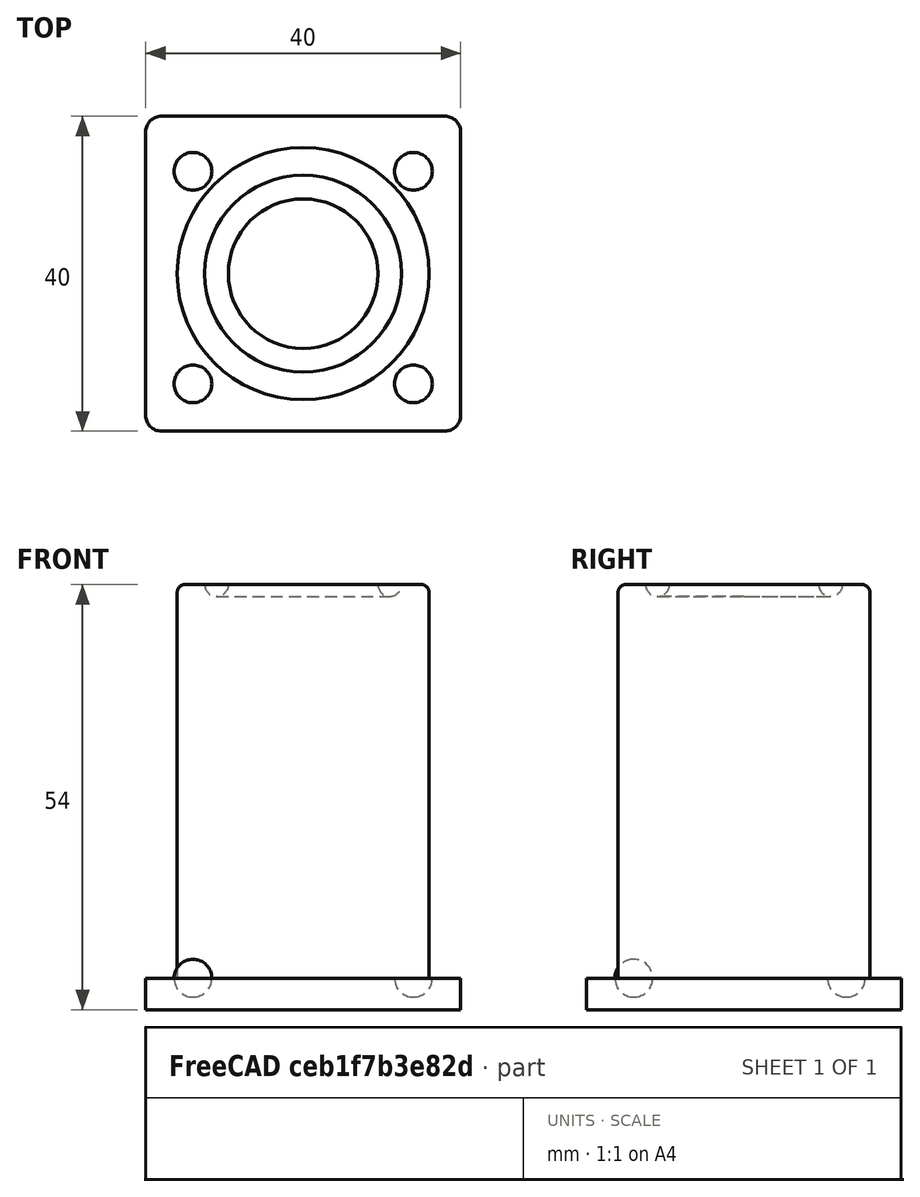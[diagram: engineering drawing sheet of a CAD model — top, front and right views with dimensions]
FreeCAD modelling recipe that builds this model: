
FCSTD DOCUMENT  (FreeCAD 1.0R39319 (Git))
Label: ojt1_t15r03_table_leg
License: All rights reserved
LicenseURL: https://en.wikipedia.org/wiki/All_rights_reserved
objects: Part::Fillet×2, Part::Cut×2, Part::Box×1, Part::Sphere×1, Part::FeaturePython×1, Part::Cylinder×1, Part::Torus×1, Part::MultiFuse×1
note: 9 computed .brp shape members not serialized (recipe doc carries the construction recipe); baked Part::Feature solids carry a one-line shape summary decoded from their .brp

FEATURE [Part::Box] Box  label="Cub"
  AttacherType = Attacher::AttachEngine3D
  Height = 4
  Length = 40
  Width = 40
FEATURE [Part::Fillet] Fillet
  Base = -> Box
  EdgeLinks = -> Box [Edge1,Edge3,Edge5,Edge7]
  Edges = 4 edges r=2: [Edge1,Edge3,Edge5,Edge7]
FEATURE [Part::Sphere] Sphere  label="Esfera"
  Angle1 = -90
  Angle2 = 90
  Angle3 = 360
  AttacherType = Attacher::AttachEngine3D
  Placement = pos=(6,6,4) rot=(0,0,1;0rad)
  Radius = 2.4
FEATURE [Part::FeaturePython] Array  # Draft array (typed FeaturePython)
  AlwaysSyncPlacement = false
  Angle = 360
  ArrayType = 0
  Axis = (0,0,1)
  Base = -> Sphere
  Center = (0,0,0)
  Count = 4
  ExpandArray = false
  Fuse = false
  IntervalAxis = (0,0,0)
  IntervalX = (28,0,0)
  IntervalY = (0,27,0)
  IntervalZ = (0,0,100)
  NumberCircles = 3
  NumberPolar = 5
  NumberX = 2
  NumberY = 2
  NumberZ = 1
  PlacementList = 4 placements: [(6,6,4),(6,33,4),(34,6,4),(34,33,4)]
  RadialDistance = 50
  ScaleList = (4) [(1,1,1),(1,1,1),(1,1,1),(1,1,1)]
  Symmetry = 1
  TangentialDistance = 25
FEATURE [Part::Cut] Cut
  Base = -> Fillet
  Refine = true
  Tool = -> Array
FEATURE [Part::Cylinder] Cylinder  label="Cilindre"
  Angle = 360
  AttacherType = Attacher::AttachEngine3D
  FirstAngle = 0
  Height = 50
  Placement = pos=(20,20,4) rot=(0,0,1;0rad)
  Radius = 16
  SecondAngle = 0
FEATURE [Part::Fillet] Fillet001
  Base = -> Cylinder
  EdgeLinks = -> Cylinder [Edge3]
  Edges = 1 edges r=1: [Edge3]
FEATURE [Part::Torus] Torus
  Angle1 = -180
  Angle2 = 180
  Angle3 = 360
  AttacherType = Attacher::AttachEngine3D
  Placement = pos=(20,20,54) rot=(0,0,1;0rad)
  Radius1 = 11
  Radius2 = 1.5
FEATURE [Part::Cut] Cut001
  Base = -> Fillet001
  Refine = true
  Tool = -> Torus
FEATURE [Part::MultiFuse] Fusion
  Refine = true
  Shapes = -> [Cut,Cut001]
